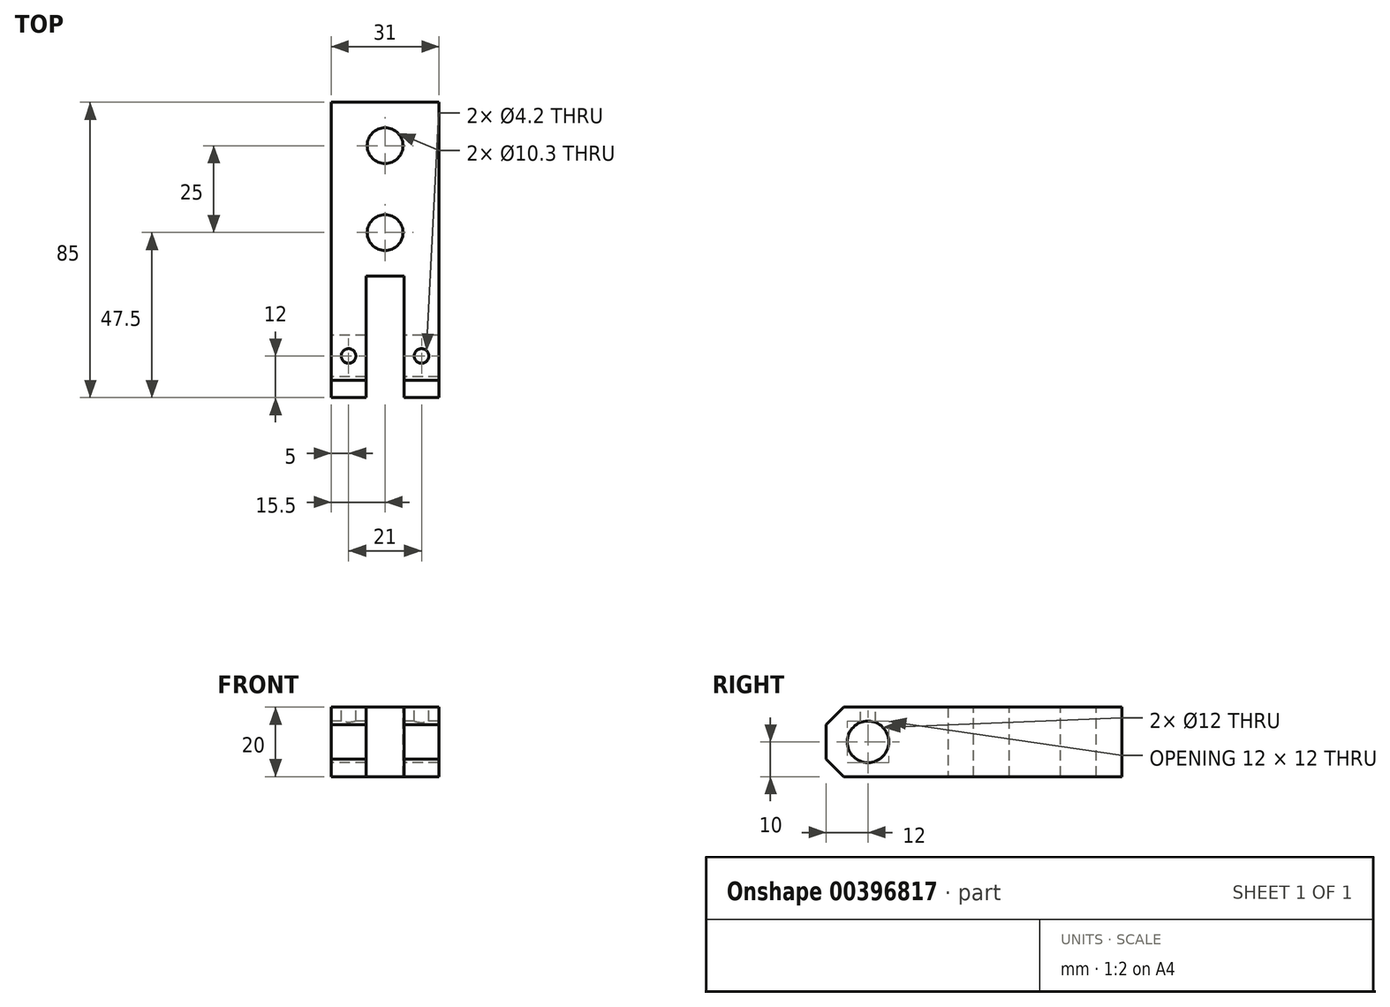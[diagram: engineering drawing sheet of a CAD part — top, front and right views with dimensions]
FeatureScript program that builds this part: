
annotation { "Feature Type Name" : "Feature", "Feature Type Description" : "" }
export const myFeature = defineFeature(function(context is Context, id is Id, definition is map)
    precondition{}
    {
        {
            var Q0;
            Q0=qCreatedBy(makeId("Top.planeOp"),FACE);
            var sketch = newSketch(context, id + "F0", { "sketchPlane" : qUnion([Q0])});
            skLineSegment(sketch, "E0", {"start": v(0, 0) * mm, "end": v(60, 0) * mm});
            skLineSegment(sketch, "E1", {"start": v(60, 0) * mm, "end": v(60, -20) * mm});
            skLineSegment(sketch, "E2", {"start": v(60, -20) * mm, "end": v(31, -20) * mm});
            skLineSegment(sketch, "E3", {"start": v(31, -20) * mm, "end": v(31, -55) * mm});
            skLineSegment(sketch, "E4", {"start": v(31, -55) * mm, "end": v(21, -55) * mm});
            skLineSegment(sketch, "E5", {"start": v(21, -55) * mm, "end": v(21, -20) * mm});
            skLineSegment(sketch, "E6", {"start": v(21, -20) * mm, "end": v(10, -20) * mm});
            skLineSegment(sketch, "E7", {"start": v(10, -20) * mm, "end": v(10, -55) * mm});
            skLineSegment(sketch, "E8", {"start": v(10, -55) * mm, "end": v(0, -55) * mm});
            skLineSegment(sketch, "E9", {"start": v(0, -55) * mm, "end": v(0, 0) * mm});
            skSolve(sketch);
        }
        {
            var Q0;
            Q0=qSketchRegion(id+"F0",true);
            extrude(context, id + "F1", {"entities" : qUnion([Q0]), "depth" : 20 * mm});
        }
        {
            var Q0;
            Q0=makeQuery(id+"F1.opExtrude","SWEPT_FACE",FACE,{"disambiguationData":[OSD([sQuery(id+"F0.wireOp",EDGE,"E9")])]});
            var sketch = newSketch(context, id + "F2", { "sketchPlane" : qUnion([Q0])});
            skPoint(sketch, "E10", {"position": v(43, 10) * mm});
            skSolve(sketch);
        }
        {
            var Q0;
            Q0=sQuery(id+"F2.wireOp",VERTEX,"E10");
            var Q1;
            Q1=makeQuery(id+"F1.opExtrude","SWEPT_BODY",BODY,{"disambiguationData":[OSD([sQuery(id+"F0.wireOp",EDGE,"E0"),sQuery(id+"F0.wireOp",EDGE,"E1"),sQuery(id+"F0.wireOp",EDGE,"E2"),sQuery(id+"F0.wireOp",EDGE,"E3"),sQuery(id+"F0.wireOp",EDGE,"E4"),sQuery(id+"F0.wireOp",EDGE,"E5"),sQuery(id+"F0.wireOp",EDGE,"E6"),sQuery(id+"F0.wireOp",EDGE,"E7"),sQuery(id+"F0.wireOp",EDGE,"E8"),sQuery(id+"F0.wireOp",EDGE,"E9")])]});
            hole(context, id + "F3", {"style" : HoleStyle.SIMPLE, "endStyle" : HoleEndStyle.THROUGH, "standardTappedOrClearance" : lookupTablePath({ "standard" : "ISO", "size" : "12", "type" : "Drilled" }), "standardBlindInLast" : lookupTablePath({ "standard" : "ISO", "size" : "12", "type" : "Drilled" }), "holeDiameter" : 12 * mm, "isTappedThrough" : true, "tappedDepth" : 12 * mm, "tapClearance" : 3, "locations" : qUnion([Q0]), "scope" : qUnion([Q1])});
        }
        {
            var Q0;
            Q0=makeQuery(id+"F1.opExtrude","CAP_FACE",FACE,{"disambiguationData":[OSD([sQuery(id+"F0.wireOp",EDGE,"E0"),sQuery(id+"F0.wireOp",EDGE,"E1"),sQuery(id+"F0.wireOp",EDGE,"E2"),sQuery(id+"F0.wireOp",EDGE,"E3"),sQuery(id+"F0.wireOp",EDGE,"E4"),sQuery(id+"F0.wireOp",EDGE,"E5"),sQuery(id+"F0.wireOp",EDGE,"E6"),sQuery(id+"F0.wireOp",EDGE,"E7"),sQuery(id+"F0.wireOp",EDGE,"E8"),sQuery(id+"F0.wireOp",EDGE,"E9")])],"isStart":false});
            var sketch = newSketch(context, id + "F4", { "sketchPlane" : qUnion([Q0])});
            skPoint(sketch, "E11", {"position": v(5, -43) * mm});
            skPoint(sketch, "E12", {"position": v(26, -43) * mm});
            skSolve(sketch);
        }
        {
            var Q0;
            Q0=sQuery(id+"F4.wireOp",VERTEX,"E11");
            var Q1;
            Q1=sQuery(id+"F4.wireOp",VERTEX,"E12");
            var Q2;
            Q2=makeQuery(id+"F1.opExtrude","SWEPT_BODY",BODY,{"disambiguationData":[OSD([sQuery(id+"F0.wireOp",EDGE,"E0"),sQuery(id+"F0.wireOp",EDGE,"E1"),sQuery(id+"F0.wireOp",EDGE,"E2"),sQuery(id+"F0.wireOp",EDGE,"E3"),sQuery(id+"F0.wireOp",EDGE,"E4"),sQuery(id+"F0.wireOp",EDGE,"E5"),sQuery(id+"F0.wireOp",EDGE,"E6"),sQuery(id+"F0.wireOp",EDGE,"E7"),sQuery(id+"F0.wireOp",EDGE,"E8"),sQuery(id+"F0.wireOp",EDGE,"E9")])]});
            hole(context, id + "F5", {"style" : HoleStyle.SIMPLE, "endStyle" : HoleEndStyle.BLIND, "standardTappedOrClearance" : lookupTablePath({ "standard" : "ISO", "engagement" : "75%", "pitch" : "0.8 mm", "size" : "M5", "type" : "Tapped" }), "standardBlindInLast" : lookupTablePath({ "standard" : "ISO", "engagement" : "75%", "pitch" : "0.8 mm", "size" : "M5", "type" : "Tapped" }), "holeDiameter" : 4.2 * mm, "showTappedDepth" : true, "holeDepth" : 14.4 * mm, "isTappedThrough" : true, "tappedDepth" : 12 * mm, "tapClearance" : 3, "locations" : qUnion([Q0, Q1]), "scope" : qUnion([Q2]), "majorDiameter" : 5 * mm});
        }
        {
            var Q0;
            Q0=makeQuery(id+"F1.opExtrude","CAP_EDGE",EDGE,{"disambiguationData":[OSD([sQuery(id+"F0.wireOp",EDGE,"E8")])],"isStart":false});
            var Q1;
            Q1=makeQuery(id+"F1.opExtrude","CAP_EDGE",EDGE,{"disambiguationData":[OSD([sQuery(id+"F0.wireOp",EDGE,"E4")])],"isStart":false});
            var Q2;
            Q2=makeQuery(id+"F1.opExtrude","CAP_EDGE",EDGE,{"disambiguationData":[OSD([sQuery(id+"F0.wireOp",EDGE,"E4")])],"isStart":true});
            var Q3;
            Q3=makeQuery(id+"F1.opExtrude","CAP_EDGE",EDGE,{"disambiguationData":[OSD([sQuery(id+"F0.wireOp",EDGE,"E8")])],"isStart":true});
            chamfer(context, id + "F6", {"entities" : qUnion([Q0, Q1, Q2, Q3]), "width" : 5 * mm, "tangentPropagation" : true});
        }
        {
            var Q0;
            Q0=makeQuery(id+"F1.opExtrude","SWEPT_FACE",FACE,{"disambiguationData":[OSD([sQuery(id+"F0.wireOp",EDGE,"E0")])]});
            var sketch = newSketch(context, id + "F7", { "sketchPlane" : qUnion([Q0])});
            skLineSegment(sketch, "E13.bottom", {"start": v(0, 0) * mm, "end": v(-60, 0) * mm});
            skLineSegment(sketch, "E13.top", {"start": v(0, 20) * mm, "end": v(-60, 20) * mm});
            skLineSegment(sketch, "E13.left", {"start": v(0, 0) * mm, "end": v(0, 20) * mm});
            skLineSegment(sketch, "E13.right", {"start": v(-60, 0) * mm, "end": v(-60, 20) * mm});
            skSolve(sketch);
        }
        {
            var Q0;
            Q0=makeQuery(id+"F7.imprint","IMPRINT",FACE,{"disambiguationData":[TD([[makeQuery(id+"F7.imprint","IMPRINT",EDGE,{"derivedFrom":sQuery(id+"F7.wireOp",EDGE,"E13.bottom")}),-1.0]])]});
            extrude(context, id + "F8", {"entities" : qUnion([Q0]), "operationType" : NewBodyOperationType.ADD, "depth" : 30 * mm});
        }
        {
            var Q0;
            Q0=makeQuery(id+"F8.boolean.opBoolean","MERGE",FACE,{"derivedFrom":[makeQuery(id+"F1.opExtrude","CAP_FACE",FACE,{"disambiguationData":[OSD([sQuery(id+"F0.wireOp",EDGE,"E0"),sQuery(id+"F0.wireOp",EDGE,"E1"),sQuery(id+"F0.wireOp",EDGE,"E2"),sQuery(id+"F0.wireOp",EDGE,"E3"),sQuery(id+"F0.wireOp",EDGE,"E4"),sQuery(id+"F0.wireOp",EDGE,"E5"),sQuery(id+"F0.wireOp",EDGE,"E6"),sQuery(id+"F0.wireOp",EDGE,"E7"),sQuery(id+"F0.wireOp",EDGE,"E8"),sQuery(id+"F0.wireOp",EDGE,"E9")])],"isStart":false}),makeQuery(id+"F8.opExtrude","SWEPT_FACE",FACE,{"disambiguationData":[OSD([sQuery(id+"F7.wireOp",EDGE,"E13.top")])]})]});
            var sketch = newSketch(context, id + "F9", { "sketchPlane" : qUnion([Q0])});
            skPoint(sketch, "E14", {"position": v(15.5, -7.5) * mm});
            skPoint(sketch, "E15", {"position": v(15.5, 17.5) * mm});
            skSolve(sketch);
        }
        {
            var Q0;
            Q0=sQuery(id+"F9.wireOp",VERTEX,"E15");
            var Q1;
            Q1=sQuery(id+"F9.wireOp",VERTEX,"E14");
            var Q2;
            Q2=makeQuery(id+"F1.opExtrude","SWEPT_BODY",BODY,{"disambiguationData":[OSD([sQuery(id+"F0.wireOp",EDGE,"E0"),sQuery(id+"F0.wireOp",EDGE,"E1"),sQuery(id+"F0.wireOp",EDGE,"E2"),sQuery(id+"F0.wireOp",EDGE,"E3"),sQuery(id+"F0.wireOp",EDGE,"E4"),sQuery(id+"F0.wireOp",EDGE,"E5"),sQuery(id+"F0.wireOp",EDGE,"E6"),sQuery(id+"F0.wireOp",EDGE,"E7"),sQuery(id+"F0.wireOp",EDGE,"E8"),sQuery(id+"F0.wireOp",EDGE,"E9")])]});
            hole(context, id + "F10", {"style" : HoleStyle.SIMPLE, "endStyle" : HoleEndStyle.THROUGH, "standardTappedOrClearance" : lookupTablePath({ "standard" : "ISO", "engagement" : "75%", "pitch" : "1.75 mm", "size" : "M12", "type" : "Tapped" }), "standardBlindInLast" : lookupTablePath({ "standard" : "ISO", "engagement" : "75%", "pitch" : "1.75 mm", "size" : "M12", "type" : "Tapped" }), "holeDiameter" : 10.3 * mm, "showTappedDepth" : true, "isTappedThrough" : true, "tappedDepth" : 12 * mm, "tapClearance" : 3, "locations" : qUnion([Q0, Q1]), "scope" : qUnion([Q2]), "majorDiameter" : 12 * mm});
        }
        {
            var Q0;
            Q0=makeQuery(id+"F8.boolean.opBoolean","MERGE",FACE,{"derivedFrom":[makeQuery(id+"F1.opExtrude","CAP_FACE",FACE,{"disambiguationData":[OSD([sQuery(id+"F0.wireOp",EDGE,"E0"),sQuery(id+"F0.wireOp",EDGE,"E1"),sQuery(id+"F0.wireOp",EDGE,"E2"),sQuery(id+"F0.wireOp",EDGE,"E3"),sQuery(id+"F0.wireOp",EDGE,"E4"),sQuery(id+"F0.wireOp",EDGE,"E5"),sQuery(id+"F0.wireOp",EDGE,"E6"),sQuery(id+"F0.wireOp",EDGE,"E7"),sQuery(id+"F0.wireOp",EDGE,"E8"),sQuery(id+"F0.wireOp",EDGE,"E9")])],"isStart":false}),makeQuery(id+"F8.opExtrude","SWEPT_FACE",FACE,{"disambiguationData":[OSD([sQuery(id+"F7.wireOp",EDGE,"E13.top")])]})]});
            var sketch = newSketch(context, id + "F11", { "sketchPlane" : qUnion([Q0])});
            skLineSegment(sketch, "E16.bottom", {"start": v(31, -20) * mm, "end": v(60, -20) * mm});
            skLineSegment(sketch, "E16.top", {"start": v(31, 30) * mm, "end": v(60, 30) * mm});
            skLineSegment(sketch, "E16.left", {"start": v(31, -20) * mm, "end": v(31, 30) * mm});
            skLineSegment(sketch, "E16.right", {"start": v(60, -20) * mm, "end": v(60, 30) * mm});
            skSolve(sketch);
        }
        {
            var Q0;
            Q0=makeQuery(id+"F11.imprint","IMPRINT",FACE,{"disambiguationData":[TD([[makeQuery(id+"F11.imprint","IMPRINT",EDGE,{"derivedFrom":sQuery(id+"F11.wireOp",EDGE,"E16.bottom")}),-1.0]])]});
            extrude(context, id + "F12", {"entities" : qUnion([Q0]), "operationType" : NewBodyOperationType.REMOVE, "endBound" : BoundingType.THROUGH_ALL, "oppositeDirection" : true, "depth" : 25 * mm});
        }
    });
